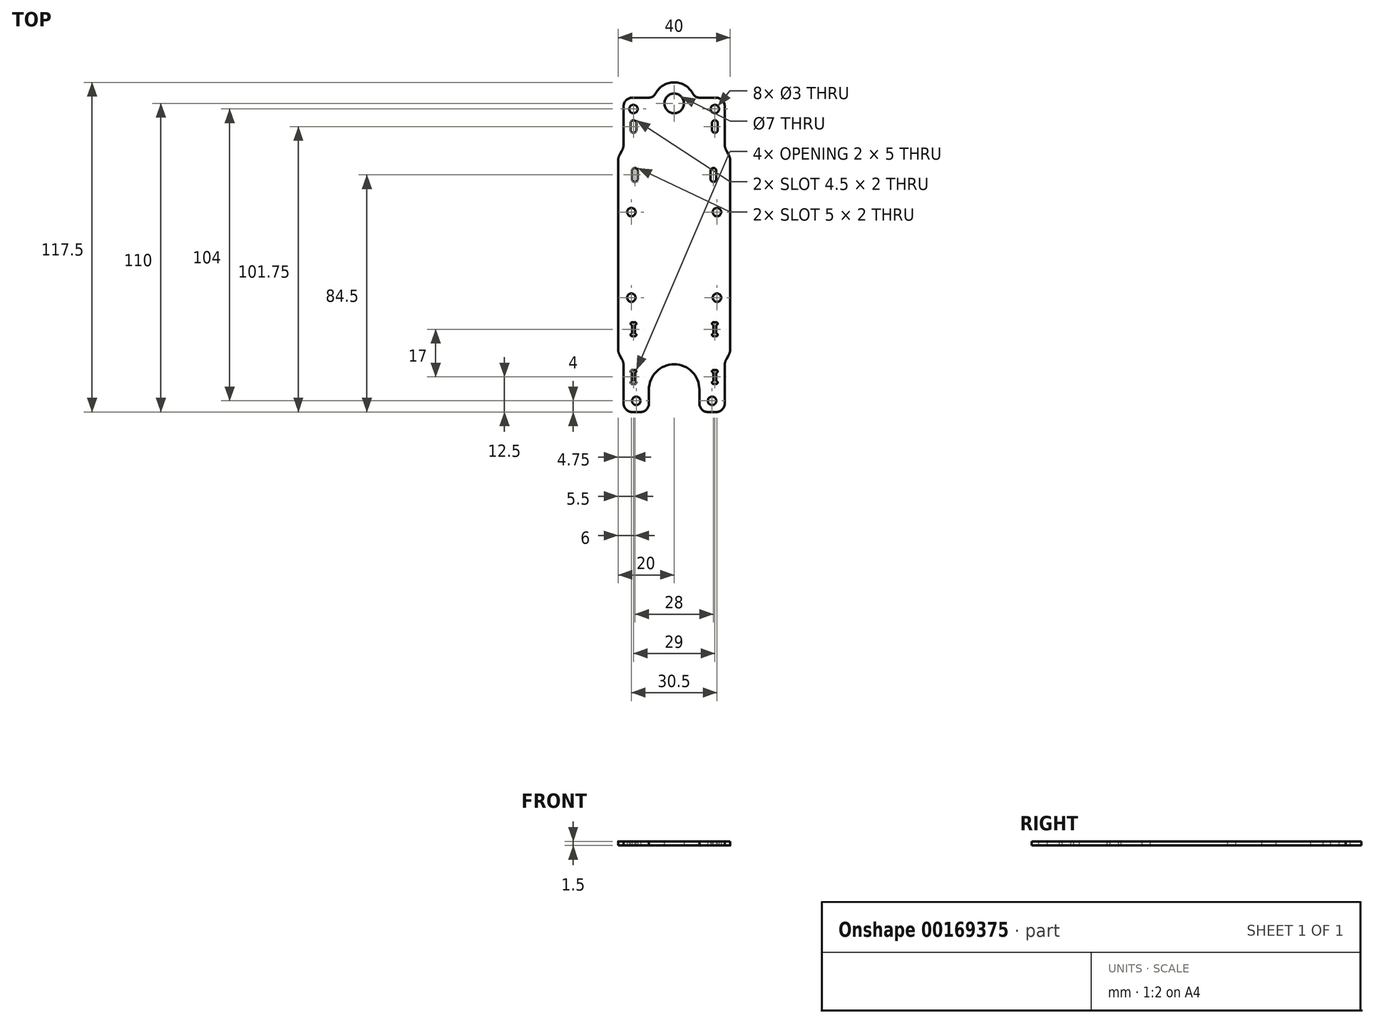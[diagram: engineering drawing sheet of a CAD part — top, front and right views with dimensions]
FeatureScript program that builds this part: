
annotation { "Feature Type Name" : "Feature", "Feature Type Description" : "" }
export const myFeature = defineFeature(function(context is Context, id is Id, definition is map)
    precondition{}
    {
        {
            var Q0;
            Q0=qCreatedBy(makeId("Top.planeOp"),FACE);
            var sketch = newSketch(context, id + "F0", { "sketchPlane" : qUnion([Q0])});
            skLineSegment(sketch, "E0.bottom", {"start": v(-15, 56) * mm, "end": v(-9.23, 56) * mm});
            skLineSegment(sketch, "E0.top", {"start": v(-15, -56) * mm, "end": v(-12, -56) * mm});
            skLineSegment(sketch, "E0.left", {"start": v(-18, 53) * mm, "end": v(-18, 38.21) * mm});
            skCircle(sketch, "E1", {"center": v(-14.5, 52) * mm, "radius": 1.5 * mm});
            skCircle(sketch, "E2.1.0.0", {"center": v(14.5, 52) * mm, "radius": 1.5 * mm});
            skLineSegment(sketch, "E2.direction1", {"start": v(-14.5, 52) * mm, "end": v(14.5, 52) * mm, "construction": true});
            skCircle(sketch, "E3", {"center": v(-13.5, -52) * mm, "radius": 1.5 * mm});
            skCircle(sketch, "E4.1.0.0", {"center": v(13.5, -52) * mm, "radius": 1.5 * mm});
            skLineSegment(sketch, "E4.direction1", {"start": v(-13.5, -52) * mm, "end": v(13.5, -52) * mm, "construction": true});
            skLineSegment(sketch, "E5", {"start": v(-9, -53) * mm, "end": v(-9, -48) * mm});
            skLineSegment(sketch, "E6", {"start": v(0, -39) * mm, "end": v(0, -39) * mm});
            skLineSegment(sketch, "E7", {"start": v(9, -48) * mm, "end": v(9, -53) * mm});
            skLineSegment(sketch, "E8.trimOffspring", {"start": v(12, -56) * mm, "end": v(15, -56) * mm});
            skPoint(sketch, "E9.visualSharp", {"position": v(-18, 56) * mm});
            skArc(sketch, "E9.filletArc", {"start": v(-15, 56) * mm, "mid": v(-17.12, 55.12) * mm, "end": v(-18, 53) * mm});
            skArc(sketch, "E10.filletArc", {"start": v(18, 53) * mm, "mid": v(17.12, 55.12) * mm, "end": v(15, 56) * mm});
            skArc(sketch, "E11.filletArc", {"start": v(-18, -53) * mm, "mid": v(-17.12, -55.12) * mm, "end": v(-15, -56) * mm});
            skArc(sketch, "E12.filletArc", {"start": v(15, -56) * mm, "mid": v(17.12, -55.12) * mm, "end": v(18, -53) * mm});
            skPoint(sketch, "E13.visualSharp", {"position": v(-9, -56) * mm});
            skArc(sketch, "E13.filletArc", {"start": v(-12, -56) * mm, "mid": v(-9.88, -55.12) * mm, "end": v(-9, -53) * mm});
            skPoint(sketch, "E14.visualSharp", {"position": v(9, -56) * mm});
            skArc(sketch, "E14.filletArc", {"start": v(9, -53) * mm, "mid": v(9.88, -55.12) * mm, "end": v(12, -56) * mm});
            skPoint(sketch, "E15.visualSharp", {"position": v(-9, -39) * mm});
            skArc(sketch, "E15.filletArc", {"start": v(0, -39) * mm, "mid": v(-6.36, -41.64) * mm, "end": v(-9, -48) * mm});
            skPoint(sketch, "E16.visualSharp", {"position": v(9, -39) * mm});
            skArc(sketch, "E16.filletArc", {"start": v(9, -48) * mm, "mid": v(6.36, -41.64) * mm, "end": v(0, -39) * mm});
            skLineSegment(sketch, "E17.left", {"start": v(-15, 30) * mm, "end": v(-15, 27) * mm});
            skLineSegment(sketch, "E17.right", {"start": v(-13, 30) * mm, "end": v(-13, 27) * mm});
            skArc(sketch, "E18", {"start": v(-13, 30) * mm, "mid": v(-14, 31) * mm, "end": v(-15, 30) * mm});
            skArc(sketch, "E19", {"start": v(-15, 27) * mm, "mid": v(-14, 26) * mm, "end": v(-13, 27) * mm});
            skLineSegment(sketch, "E20", {"start": v(-14, 30) * mm, "end": v(-14, 27) * mm, "construction": true});
            skLineSegment(sketch, "E21.MirrorCS", {"start": v(14, 30) * mm, "end": v(14, 27) * mm, "construction": true});
            skLineSegment(sketch, "E22.MirrorCS", {"start": v(13, 30) * mm, "end": v(13, 27) * mm});
            skArc(sketch, "E23.MirrorCS", {"start": v(15, 27) * mm, "mid": v(14, 26) * mm, "end": v(13, 27) * mm});
            skArc(sketch, "E24.MirrorCS", {"start": v(13, 30) * mm, "mid": v(14, 31) * mm, "end": v(15, 30) * mm});
            skLineSegment(sketch, "E25.MirrorCS", {"start": v(15, 30) * mm, "end": v(15, 27) * mm});
            skCircle(sketch, "E26", {"center": v(0, 54) * mm, "radius": 3.5 * mm});
            skCircle(sketch, "E27", {"center": v(-15.25, -15.25) * mm, "radius": 1.5 * mm});
            skCircle(sketch, "E28.0.1.0", {"center": v(-15.25, 15.25) * mm, "radius": 1.5 * mm});
            skLineSegment(sketch, "E28.direction1", {"start": v(-15.25, -15.25) * mm, "end": v(15.25, -15.25) * mm, "construction": true});
            skLineSegment(sketch, "E28.direction2", {"start": v(-15.25, -15.25) * mm, "end": v(-15.25, 15.25) * mm, "construction": true});
            skArc(sketch, "E29", {"start": v(6.6, 57.57) * mm, "mid": v(0, 61.5) * mm, "end": v(-6.6, 57.57) * mm});
            skLineSegment(sketch, "E30.trimOffspring", {"start": v(9.23, 56) * mm, "end": v(15, 56) * mm});
            skPoint(sketch, "E31.visualSharp", {"position": v(-7.23, 56) * mm});
            skArc(sketch, "E31.filletArc", {"start": v(-9.23, 56) * mm, "mid": v(-7.7, 56.42) * mm, "end": v(-6.6, 57.57) * mm});
            skPoint(sketch, "E32.visualSharp", {"position": v(7.23, 56) * mm});
            skArc(sketch, "E32.filletArc", {"start": v(6.6, 57.57) * mm, "mid": v(7.7, 56.42) * mm, "end": v(9.23, 56) * mm});
            skLineSegment(sketch, "E33", {"start": v(18, 53) * mm, "end": v(18, 38.21) * mm});
            skCircle(sketch, "E34", {"center": v(15.25, -15.25) * mm, "radius": 1.5 * mm});
            skLineSegment(sketch, "E35", {"start": v(-15.25, 15.25) * mm, "end": v(15.25, 15.25) * mm, "construction": true});
            skLineSegment(sketch, "E36", {"start": v(15.25, -15.25) * mm, "end": v(15.25, 15.25) * mm, "construction": true});
            skCircle(sketch, "E37", {"center": v(15.25, 15.25) * mm, "radius": 1.5 * mm});
            skLineSegment(sketch, "E38.trimOffspring", {"start": v(-18, -38.21) * mm, "end": v(-18, -53) * mm});
            skLineSegment(sketch, "E39.trimOffspring", {"start": v(18, -38.21) * mm, "end": v(18, -53) * mm});
            skLineSegment(sketch, "E40", {"start": v(-20, 34.75) * mm, "end": v(-20, -34.75) * mm});
            skLineSegment(sketch, "E41", {"start": v(20, 34.75) * mm, "end": v(20, -34.75) * mm});
            skLineSegment(sketch, "E42", {"start": v(-13, 30) * mm, "end": v(-15, 30) * mm, "construction": true});
            skLineSegment(sketch, "E43", {"start": v(-20, 34.75) * mm, "end": v(-18, 38.21) * mm});
            skLineSegment(sketch, "E44", {"start": v(20, 34.75) * mm, "end": v(18, 38.21) * mm});
            skLineSegment(sketch, "E45", {"start": v(-20, -34.75) * mm, "end": v(-18, -38.21) * mm});
            skLineSegment(sketch, "E46", {"start": v(20, -34.75) * mm, "end": v(18, -38.21) * mm});
            skSolve(sketch);
        }
        {
            var Q0;
            Q0 = qSketchRegion(id + "F0", true);
            extrude(context, id + "F1", {"entities" : qUnion([Q0]), "depth" : 1.5 * mm});
        }
        {
            var Q0;
            Q0=makeQuery(id+"F1.opExtrude","CAP_FACE",FACE,{"disambiguationData":[OSD([sQuery(id+"F0.wireOp",EDGE,"E0.bottom"),sQuery(id+"F0.wireOp",EDGE,"E0.top"),sQuery(id+"F0.wireOp",EDGE,"E0.left"),sQuery(id+"F0.wireOp",EDGE,"E0.right"),sQuery(id+"F0.wireOp",EDGE,"E1"),sQuery(id+"F0.wireOp",EDGE,"E2.1.0.0"),sQuery(id+"F0.wireOp",EDGE,"E3"),sQuery(id+"F0.wireOp",EDGE,"E4.1.0.0"),sQuery(id+"F0.wireOp",EDGE,"E5"),sQuery(id+"F0.wireOp",EDGE,"E6"),sQuery(id+"F0.wireOp",EDGE,"E7"),sQuery(id+"F0.wireOp",EDGE,"E8.trimOffspring"),sQuery(id+"F0.wireOp",EDGE,"An8G2rTH-zNnP-4HBr-A43H-9DaWRu82Fl5K"),sQuery(id+"F0.wireOp",EDGE,"y7juZOuk-tiEO-DqVY-Ryo9-o0FS7rlak0DI"),sQuery(id+"F0.wireOp",EDGE,"orcC2HSU-W3PP-IXOJ-rwP4-cDMbfmOT231B"),sQuery(id+"F0.wireOp",EDGE,"ql8vDpUL-cG70-PS0W-HVP0-FYVPeRxEgrYR"),sQuery(id+"F0.wireOp",EDGE,"qFBB1RLD-MdjJ-3Uil-oXsZ-DPSsT7MBtBmP"),sQuery(id+"F0.wireOp",EDGE,"ashqnSfA-S9f8-otR1-AVUh-4qhQMrLSiuGh"),sQuery(id+"F0.wireOp",EDGE,"bb509eea-203c-45f5-bfbb-c370d285206a.trimOffspring"),sQuery(id+"F0.wireOp",EDGE,"126af195-25f6-4e34-91c2-7912d32c8cf6.trimOffspring"),sQuery(id+"F0.wireOp",EDGE,"E9.filletArc"),sQuery(id+"F0.wireOp",EDGE,"E10.filletArc"),sQuery(id+"F0.wireOp",EDGE,"E11.filletArc"),sQuery(id+"F0.wireOp",EDGE,"E12.filletArc"),sQuery(id+"F0.wireOp",EDGE,"E13.filletArc"),sQuery(id+"F0.wireOp",EDGE,"E14.filletArc"),sQuery(id+"F0.wireOp",EDGE,"ef886a1c-e68f-404b-ab2c-7ee09a2b5bbe.filletArc"),sQuery(id+"F0.wireOp",EDGE,"414a852e-731d-4295-b6e3-d029fca2ddd6.filletArc"),sQuery(id+"F0.wireOp",EDGE,"92759fa6-c394-4f99-9076-5869bb745d13.filletArc"),sQuery(id+"F0.wireOp",EDGE,"e44b0f4d-2ab9-4c8f-a137-660ef34945d7.filletArc"),sQuery(id+"F0.wireOp",EDGE,"f379995e-1a42-435a-a7b2-4a25e13e0786.filletArc"),sQuery(id+"F0.wireOp",EDGE,"a38adbaf-9326-4f05-bf34-7300b6c6fa8e.filletArc"),sQuery(id+"F0.wireOp",EDGE,"c50125da-e0a7-4a8d-8189-266b844f160a.filletArc"),sQuery(id+"F0.wireOp",EDGE,"729702d7-74d0-46d4-9f2b-10edec5f556c.filletArc"),sQuery(id+"F0.wireOp",EDGE,"E15.filletArc"),sQuery(id+"F0.wireOp",EDGE,"E16.filletArc"),sQuery(id+"F0.wireOp",EDGE,"E17.left"),sQuery(id+"F0.wireOp",EDGE,"E17.right"),sQuery(id+"F0.wireOp",EDGE,"E18"),sQuery(id+"F0.wireOp",EDGE,"E19"),sQuery(id+"F0.wireOp",EDGE,"E22.MirrorCS"),sQuery(id+"F0.wireOp",EDGE,"E23.MirrorCS"),sQuery(id+"F0.wireOp",EDGE,"E24.MirrorCS"),sQuery(id+"F0.wireOp",EDGE,"E25.MirrorCS"),sQuery(id+"F0.wireOp",EDGE,"E26"),sQuery(id+"F0.wireOp",EDGE,"E27"),sQuery(id+"F0.wireOp",EDGE,"E28.0.1.0"),sQuery(id+"F0.wireOp",EDGE,"E28.1.0.0"),sQuery(id+"F0.wireOp",EDGE,"E28.1.1.0")])],"isStart":false});
            var sketch = newSketch(context, id + "F2", { "sketchPlane" : qUnion([Q0])});
            skLineSegment(sketch, "E47.bottom", {"start": v(-15, -41) * mm, "end": v(-14, -41) * mm});
            skLineSegment(sketch, "E47.top", {"start": v(-15, -46) * mm, "end": v(-14, -46) * mm});
            skLineSegment(sketch, "E47.left", {"start": v(-15, -42) * mm, "end": v(-15, -45) * mm});
            skLineSegment(sketch, "E47.right", {"start": v(-14, -42) * mm, "end": v(-14, -45) * mm});
            skArc(sketch, "E48", {"start": v(-14, -46) * mm, "mid": v(-13.5, -45.5) * mm, "end": v(-14, -45) * mm});
            skArc(sketch, "E49", {"start": v(-15, -45) * mm, "mid": v(-15.5, -45.5) * mm, "end": v(-15, -46) * mm});
            skArc(sketch, "E50", {"start": v(-14, -42) * mm, "mid": v(-13.5, -41.5) * mm, "end": v(-14, -41) * mm});
            skArc(sketch, "E51", {"start": v(-15, -41) * mm, "mid": v(-15.5, -41.5) * mm, "end": v(-15, -42) * mm});
            skLineSegment(sketch, "E52.bottom", {"start": v(-15, -24) * mm, "end": v(-14, -24) * mm});
            skLineSegment(sketch, "E52.top", {"start": v(-15, -29) * mm, "end": v(-14, -29) * mm});
            skLineSegment(sketch, "E52.right", {"start": v(-14, -25) * mm, "end": v(-14, -28) * mm});
            skArc(sketch, "E53", {"start": v(-14, -29) * mm, "mid": v(-13.5, -28.5) * mm, "end": v(-14, -28) * mm});
            skArc(sketch, "E54", {"start": v(-15, -28) * mm, "mid": v(-15.5, -28.5) * mm, "end": v(-15, -29) * mm});
            skArc(sketch, "E55", {"start": v(-14, -25) * mm, "mid": v(-13.5, -24.5) * mm, "end": v(-14, -24) * mm});
            skArc(sketch, "E56", {"start": v(-15, -24) * mm, "mid": v(-15.5, -24.5) * mm, "end": v(-15, -25) * mm});
            skLineSegment(sketch, "E57.trimOffspring", {"start": v(-15, -25) * mm, "end": v(-15, -28) * mm});
            skArc(sketch, "E58.MirrorCS", {"start": v(15, -28) * mm, "mid": v(15.5, -28.5) * mm, "end": v(15, -29) * mm});
            skLineSegment(sketch, "E59.MirrorCS", {"start": v(15, -46) * mm, "end": v(14, -46) * mm});
            skLineSegment(sketch, "E60.MirrorCS", {"start": v(15, -29) * mm, "end": v(14, -29) * mm});
            skLineSegment(sketch, "E61.MirrorCS", {"start": v(15, -41) * mm, "end": v(14, -41) * mm});
            skArc(sketch, "E62.MirrorCS", {"start": v(15, -45) * mm, "mid": v(15.5, -45.5) * mm, "end": v(15, -46) * mm});
            skArc(sketch, "E63.MirrorCS", {"start": v(14, -42) * mm, "mid": v(13.5, -41.5) * mm, "end": v(14, -41) * mm});
            skArc(sketch, "E64.MirrorCS", {"start": v(14, -29) * mm, "mid": v(13.5, -28.5) * mm, "end": v(14, -28) * mm});
            skArc(sketch, "E65.MirrorCS", {"start": v(14, -46) * mm, "mid": v(13.5, -45.5) * mm, "end": v(14, -45) * mm});
            skArc(sketch, "E66.MirrorCS", {"start": v(15, -24) * mm, "mid": v(15.5, -24.5) * mm, "end": v(15, -25) * mm});
            skArc(sketch, "E67.MirrorCS", {"start": v(14, -25) * mm, "mid": v(13.5, -24.5) * mm, "end": v(14, -24) * mm});
            skLineSegment(sketch, "E68.MirrorCS", {"start": v(15, -24) * mm, "end": v(14, -24) * mm});
            skArc(sketch, "E69.MirrorCS", {"start": v(15, -41) * mm, "mid": v(15.5, -41.5) * mm, "end": v(15, -42) * mm});
            skLineSegment(sketch, "E70.MirrorCS", {"start": v(15, -42) * mm, "end": v(15, -45) * mm});
            skLineSegment(sketch, "E71.MirrorCS", {"start": v(14, -25) * mm, "end": v(14, -28) * mm});
            skLineSegment(sketch, "E72.MirrorCS", {"start": v(14, -42) * mm, "end": v(14, -45) * mm});
            skLineSegment(sketch, "E73.MirrorCS", {"start": v(15, -25) * mm, "end": v(15, -28) * mm});
            skSolve(sketch);
        }
        {
            var Q0;
            Q0 = qSketchRegion(id + "F2", true);
            extrude(context, id + "F3", {"entities" : qUnion([Q0]), "operationType" : NewBodyOperationType.REMOVE, "endBound" : BoundingType.THROUGH_ALL, "oppositeDirection" : true, "depth" : 25 * mm});
        }
        {
            var Q0;
            Q0=makeQuery(id+"F1.opExtrude","CAP_FACE",FACE,{"disambiguationData":[OSD([sQuery(id+"F0.wireOp",EDGE,"E0.bottom"),sQuery(id+"F0.wireOp",EDGE,"E0.top"),sQuery(id+"F0.wireOp",EDGE,"E0.left"),sQuery(id+"F0.wireOp",EDGE,"E0.right"),sQuery(id+"F0.wireOp",EDGE,"E1"),sQuery(id+"F0.wireOp",EDGE,"E2.1.0.0"),sQuery(id+"F0.wireOp",EDGE,"E3"),sQuery(id+"F0.wireOp",EDGE,"E4.1.0.0"),sQuery(id+"F0.wireOp",EDGE,"E5"),sQuery(id+"F0.wireOp",EDGE,"E6"),sQuery(id+"F0.wireOp",EDGE,"E7"),sQuery(id+"F0.wireOp",EDGE,"E8.trimOffspring"),sQuery(id+"F0.wireOp",EDGE,"An8G2rTH-zNnP-4HBr-A43H-9DaWRu82Fl5K"),sQuery(id+"F0.wireOp",EDGE,"y7juZOuk-tiEO-DqVY-Ryo9-o0FS7rlak0DI"),sQuery(id+"F0.wireOp",EDGE,"orcC2HSU-W3PP-IXOJ-rwP4-cDMbfmOT231B"),sQuery(id+"F0.wireOp",EDGE,"ql8vDpUL-cG70-PS0W-HVP0-FYVPeRxEgrYR"),sQuery(id+"F0.wireOp",EDGE,"qFBB1RLD-MdjJ-3Uil-oXsZ-DPSsT7MBtBmP"),sQuery(id+"F0.wireOp",EDGE,"ashqnSfA-S9f8-otR1-AVUh-4qhQMrLSiuGh"),sQuery(id+"F0.wireOp",EDGE,"bb509eea-203c-45f5-bfbb-c370d285206a.trimOffspring"),sQuery(id+"F0.wireOp",EDGE,"126af195-25f6-4e34-91c2-7912d32c8cf6.trimOffspring"),sQuery(id+"F0.wireOp",EDGE,"E9.filletArc"),sQuery(id+"F0.wireOp",EDGE,"E10.filletArc"),sQuery(id+"F0.wireOp",EDGE,"E11.filletArc"),sQuery(id+"F0.wireOp",EDGE,"E12.filletArc"),sQuery(id+"F0.wireOp",EDGE,"E13.filletArc"),sQuery(id+"F0.wireOp",EDGE,"E14.filletArc"),sQuery(id+"F0.wireOp",EDGE,"ef886a1c-e68f-404b-ab2c-7ee09a2b5bbe.filletArc"),sQuery(id+"F0.wireOp",EDGE,"414a852e-731d-4295-b6e3-d029fca2ddd6.filletArc"),sQuery(id+"F0.wireOp",EDGE,"92759fa6-c394-4f99-9076-5869bb745d13.filletArc"),sQuery(id+"F0.wireOp",EDGE,"e44b0f4d-2ab9-4c8f-a137-660ef34945d7.filletArc"),sQuery(id+"F0.wireOp",EDGE,"f379995e-1a42-435a-a7b2-4a25e13e0786.filletArc"),sQuery(id+"F0.wireOp",EDGE,"a38adbaf-9326-4f05-bf34-7300b6c6fa8e.filletArc"),sQuery(id+"F0.wireOp",EDGE,"c50125da-e0a7-4a8d-8189-266b844f160a.filletArc"),sQuery(id+"F0.wireOp",EDGE,"729702d7-74d0-46d4-9f2b-10edec5f556c.filletArc"),sQuery(id+"F0.wireOp",EDGE,"E15.filletArc"),sQuery(id+"F0.wireOp",EDGE,"E16.filletArc"),sQuery(id+"F0.wireOp",EDGE,"E17.left"),sQuery(id+"F0.wireOp",EDGE,"E17.right"),sQuery(id+"F0.wireOp",EDGE,"E18"),sQuery(id+"F0.wireOp",EDGE,"E19"),sQuery(id+"F0.wireOp",EDGE,"E22.MirrorCS"),sQuery(id+"F0.wireOp",EDGE,"E23.MirrorCS"),sQuery(id+"F0.wireOp",EDGE,"E24.MirrorCS"),sQuery(id+"F0.wireOp",EDGE,"E25.MirrorCS"),sQuery(id+"F0.wireOp",EDGE,"E26"),sQuery(id+"F0.wireOp",EDGE,"E27"),sQuery(id+"F0.wireOp",EDGE,"E28.0.1.0"),sQuery(id+"F0.wireOp",EDGE,"E28.1.0.0"),sQuery(id+"F0.wireOp",EDGE,"E28.1.1.0")])],"isStart":false});
            var sketch = newSketch(context, id + "F4", { "sketchPlane" : qUnion([Q0])});
            skArc(sketch, "E74", {"start": v(-13.5, 47) * mm, "mid": v(-14.5, 48) * mm, "end": v(-15.5, 47) * mm});
            skArc(sketch, "E75", {"start": v(-15.5, 44.5) * mm, "mid": v(-14.5, 43.5) * mm, "end": v(-13.5, 44.5) * mm});
            skLineSegment(sketch, "E76", {"start": v(-14.5, 47) * mm, "end": v(-14.5, 44.5) * mm, "construction": true});
            skLineSegment(sketch, "E77", {"start": v(-15.5, 47) * mm, "end": v(-15.5, 44.5) * mm});
            skLineSegment(sketch, "E78", {"start": v(-13.5, 47) * mm, "end": v(-13.5, 44.5) * mm});
            skArc(sketch, "E79.MirrorCS", {"start": v(13.5, 47) * mm, "mid": v(14.5, 48) * mm, "end": v(15.5, 47) * mm});
            skArc(sketch, "E80.MirrorCS", {"start": v(15.5, 44.5) * mm, "mid": v(14.5, 43.5) * mm, "end": v(13.5, 44.5) * mm});
            skLineSegment(sketch, "E81.MirrorCS", {"start": v(14.5, 47) * mm, "end": v(14.5, 44.5) * mm, "construction": true});
            skLineSegment(sketch, "E82.MirrorCS", {"start": v(15.5, 47) * mm, "end": v(15.5, 44.5) * mm});
            skLineSegment(sketch, "E83.MirrorCS", {"start": v(13.5, 47) * mm, "end": v(13.5, 44.5) * mm});
            skSolve(sketch);
        }
        {
            var Q0;
            Q0 = qSketchRegion(id + "F4", true);
            extrude(context, id + "F5", {"entities" : qUnion([Q0]), "operationType" : NewBodyOperationType.REMOVE, "endBound" : BoundingType.THROUGH_ALL, "oppositeDirection" : true, "depth" : 25 * mm});
        }
        {
            var Q0;
            Q0=makeQuery(id+"F1.opExtrude","SWEPT_EDGE",EDGE,{"disambiguationData":[OSD([sQuery(id+"F0.wireOp",EDGE,"E40"),sQuery(id+"F0.wireOp",EDGE,"E43")])]});
            var Q1;
            Q1=makeQuery(id+"F1.opExtrude","SWEPT_EDGE",EDGE,{"disambiguationData":[OSD([sQuery(id+"F0.wireOp",EDGE,"E41"),sQuery(id+"F0.wireOp",EDGE,"E44")])]});
            var Q2;
            Q2=makeQuery(id+"F1.opExtrude","SWEPT_EDGE",EDGE,{"disambiguationData":[OSD([sQuery(id+"F0.wireOp",EDGE,"E41"),sQuery(id+"F0.wireOp",EDGE,"E46")])]});
            var Q3;
            Q3=makeQuery(id+"F1.opExtrude","SWEPT_EDGE",EDGE,{"disambiguationData":[OSD([sQuery(id+"F0.wireOp",EDGE,"E40"),sQuery(id+"F0.wireOp",EDGE,"E45")])]});
            var Q4;
            Q4=makeQuery(id+"F1.opExtrude","SWEPT_EDGE",EDGE,{"disambiguationData":[OSD([sQuery(id+"F0.wireOp",EDGE,"E38.trimOffspring"),sQuery(id+"F0.wireOp",EDGE,"E45")])]});
            var Q5;
            Q5=makeQuery(id+"F1.opExtrude","SWEPT_EDGE",EDGE,{"disambiguationData":[OSD([sQuery(id+"F0.wireOp",EDGE,"E39.trimOffspring"),sQuery(id+"F0.wireOp",EDGE,"E46")])]});
            var Q6;
            Q6=makeQuery(id+"F1.opExtrude","SWEPT_EDGE",EDGE,{"disambiguationData":[OSD([sQuery(id+"F0.wireOp",EDGE,"E33"),sQuery(id+"F0.wireOp",EDGE,"E44")])]});
            var Q7;
            Q7=makeQuery(id+"F1.opExtrude","SWEPT_EDGE",EDGE,{"disambiguationData":[OSD([sQuery(id+"F0.wireOp",EDGE,"E0.left"),sQuery(id+"F0.wireOp",EDGE,"E43")])]});
            fillet(context, id + "F6", {"entities" : qUnion([Q0, Q1, Q2, Q3, Q4, Q5, Q6, Q7]), "radius" : 5 * mm, "tangentPropagation" : true, "allowEdgeOverflow" : false});
        }
    });
